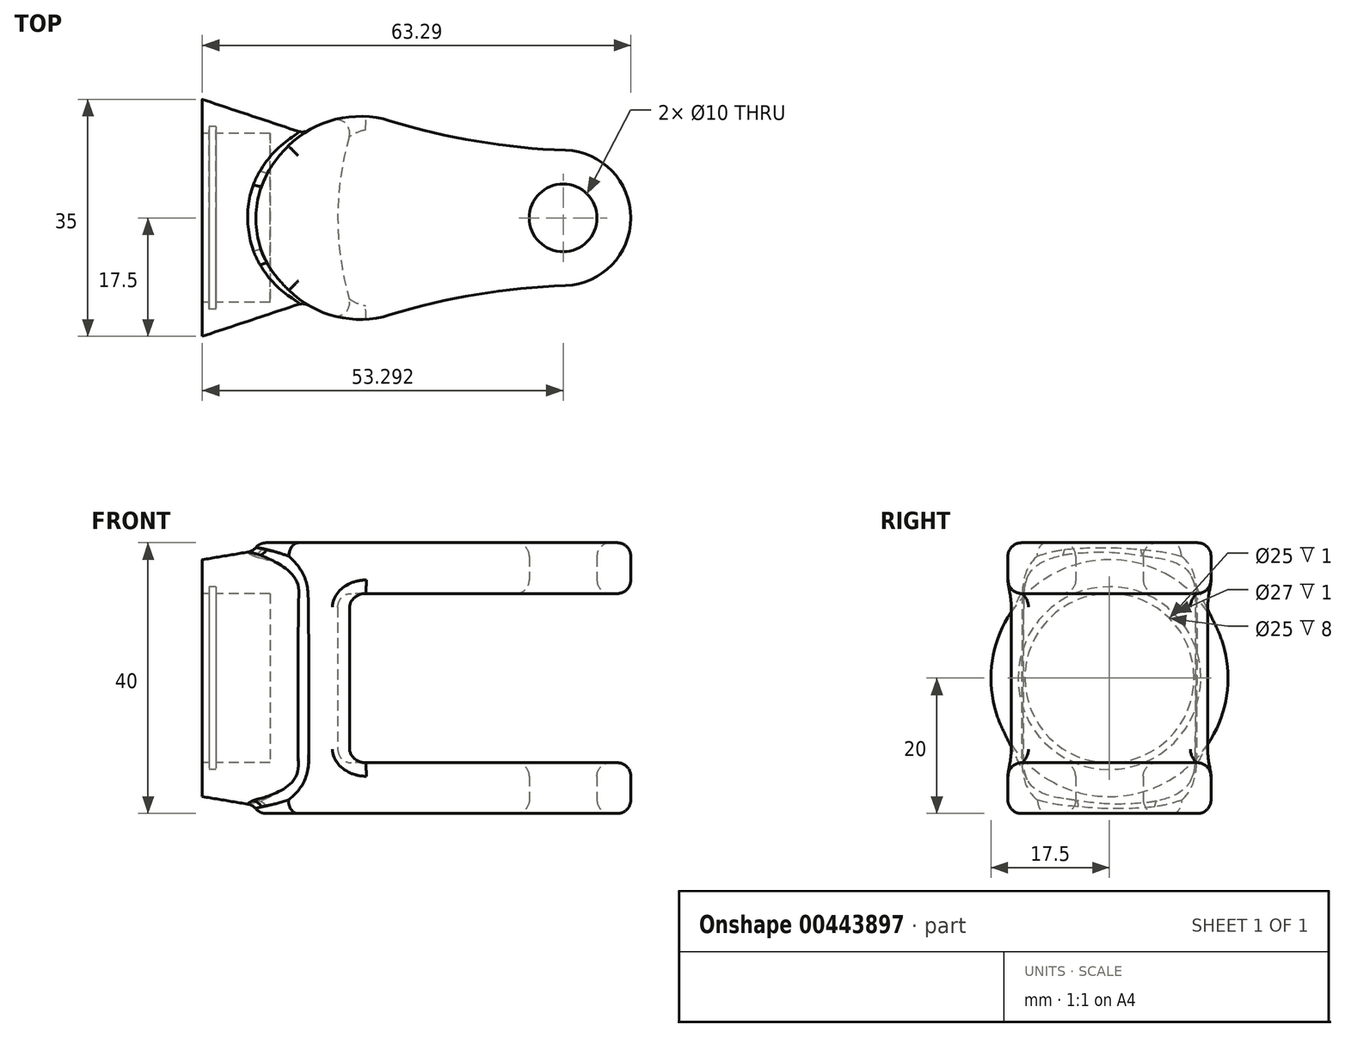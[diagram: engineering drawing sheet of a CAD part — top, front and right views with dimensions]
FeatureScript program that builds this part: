
annotation { "Feature Type Name" : "Feature", "Feature Type Description" : "" }
export const myFeature = defineFeature(function(context is Context, id is Id, definition is map)
    precondition{}
    {
        {
            var Q0;
            Q0=qCreatedBy(makeId("Right.planeOp"),FACE);
            var sketch = newSketch(context, id + "F0", { "sketchPlane" : qUnion([Q0])});
            skCircle(sketch, "E0", {"center": v(0, 0) * mm, "radius": 17.5 * mm});
            skSolve(sketch);
        }
        {
            var Q0;
            Q0=qCreatedBy(makeId("Right.planeOp"),FACE);
            cPlane(context, id + "F1", {"entities" : qUnion([Q0]), "cplaneType" : CPlaneType.OFFSET, "offset" : 15 * mm, "width" : 150 * mm, "height" : 150 * mm});
        }
        {
            var Q0;
            Q0=qCreatedBy(id+"F1.planeOp",FACE);
            var sketch = newSketch(context, id + "F2", { "sketchPlane" : qUnion([Q0])});
            skLineSegment(sketch, "E1.bottom", {"start": v(-5, 20) * mm, "end": v(5, 20) * mm});
            skLineSegment(sketch, "E1.top", {"start": v(-5, -20) * mm, "end": v(5, -20) * mm});
            skLineSegment(sketch, "E1.left", {"start": v(-12.5, 12.5) * mm, "end": v(-12.5, -12.5) * mm});
            skLineSegment(sketch, "E1.right", {"start": v(12.5, 12.5) * mm, "end": v(12.5, -12.5) * mm});
            skPoint(sketch, "E1.middle", {"position": v(0, 0) * mm});
            skPoint(sketch, "E2.visualSharp", {"position": v(-12.5, 20) * mm});
            skArc(sketch, "E2.filletArc", {"start": v(-5, 20) * mm, "mid": v(-10.3, 17.8) * mm, "end": v(-12.5, 12.5) * mm});
            skPoint(sketch, "E3.visualSharp", {"position": v(12.5, 20) * mm});
            skArc(sketch, "E3.filletArc", {"start": v(12.5, 12.5) * mm, "mid": v(10.3, 17.8) * mm, "end": v(5, 20) * mm});
            skPoint(sketch, "E4.visualSharp", {"position": v(12.5, -20) * mm});
            skArc(sketch, "E4.filletArc", {"start": v(5, -20) * mm, "mid": v(10.3, -17.8) * mm, "end": v(12.5, -12.5) * mm});
            skPoint(sketch, "E5.visualSharp", {"position": v(-12.5, -20) * mm});
            skArc(sketch, "E5.filletArc", {"start": v(-12.5, -12.5) * mm, "mid": v(-10.3, -17.8) * mm, "end": v(-5, -20) * mm});
            skSolve(sketch);
        }
        {
            var Q0;
            Q0=makeQuery(id+"F0.imprint","IMPRINT",FACE,{"disambiguationData":[TD([[makeQuery(id+"F0.imprint","IMPRINT",EDGE,{"derivedFrom":sQuery(id+"F0.wireOp",EDGE,"E0")}),1.0]])]});
            var Q1;
            Q1=makeQuery(id+"F2.imprint","IMPRINT",FACE,{"disambiguationData":[TD([[makeQuery(id+"F2.imprint","IMPRINT",EDGE,{"derivedFrom":sQuery(id+"F2.wireOp",EDGE,"E1.bottom")}),-1.0]])]});
            loft(context, id + "F3", {"sheetProfilesArray" : [{ "sheetProfileEntities" : qUnion([Q0]) }, { "sheetProfileEntities" : qUnion([Q1]) }]});
        }
        {
            var Q0;
            Q0=qCreatedBy(makeId("Top.planeOp"),FACE);
            var sketch = newSketch(context, id + "F4", { "sketchPlane" : qUnion([Q0])});
            skCircle(sketch, "E6", {"center": v(23.3, 0) * mm, "radius": 15 * mm});
            skCircle(sketch, "E7", {"center": v(53.3, 0) * mm, "radius": 10 * mm});
            skArc(sketch, "E8", {"start": v(27.7, -14.34) * mm, "mid": v(40.52, -11.31) * mm, "end": v(53.63, -10) * mm});
            skArc(sketch, "E9", {"start": v(27.7, 14.34) * mm, "mid": v(40.52, 11.31) * mm, "end": v(53.63, 10) * mm});
            skSolve(sketch);
        }
        {
            var Q0;
            Q0 = qSketchRegion(id + "F4", true);
            extrude(context, id + "F5", {"entities" : qUnion([Q0]), "operationType" : NewBodyOperationType.ADD, "endBound" : BoundingType.SYMMETRIC, "depth" : 40 * mm});
        }
        {
            var Q0;
            Q0=qCreatedBy(makeId("Front.planeOp"),FACE);
            var sketch = newSketch(context, id + "F6", { "sketchPlane" : qUnion([Q0])});
            skLineSegment(sketch, "E10.0.0", {"start": v(53.63, -20) * mm, "end": v(63.3, -20) * mm});
            skLineSegment(sketch, "E10.0.1", {"start": v(53.63, -20) * mm, "end": v(53.63, 20) * mm});
            skLineSegment(sketch, "E10.0.2", {"start": v(53.63, 20) * mm, "end": v(63.3, 20) * mm});
            skLineSegment(sketch, "E10.0.3", {"start": v(53.63, 20) * mm, "end": v(53.63, -20) * mm});
            skLineSegment(sketch, "E11.bottom", {"start": v(63.3, 12.5) * mm, "end": v(20, 12.5) * mm});
            skLineSegment(sketch, "E11.top", {"start": v(63.3, -12.5) * mm, "end": v(20, -12.5) * mm});
            skLineSegment(sketch, "E11.left", {"start": v(63.3, 12.5) * mm, "end": v(63.3, -12.5) * mm});
            skLineSegment(sketch, "E11.right", {"start": v(20, 12.5) * mm, "end": v(20, -12.5) * mm});
            skSolve(sketch);
        }
        {
            var Q0;
            Q0 = qSketchRegion(id + "F6", true);
            var Q1;
            Q1=sQuery(id+"F6.wireOp",EDGE,"E11.left");
            revolve(context, id + "F7", {"operationType" : NewBodyOperationType.REMOVE, "entities" : qUnion([Q0]), "axis" : qUnion([Q1]), "revolveType" : RevolveType.FULL, "oppositeDirection" : true});
        }
        {
            var Q0;
            Q0=makeQuery(id+"F3.opLoft","CAP_FACE",FACE,{"disambiguationData":[OSD([makeQuery(id+"F0.imprint","IMPRINT",FACE,{"disambiguationData":[TD([[makeQuery(id+"F0.imprint","IMPRINT",EDGE,{"derivedFrom":sQuery(id+"F0.wireOp",EDGE,"E0")}),1.0]])]})])],"isStart":true});
            var sketch = newSketch(context, id + "F8", { "sketchPlane" : qUnion([Q0])});
            skCircle(sketch, "E12", {"center": v(0, 0) * mm, "radius": 12.5 * mm});
            skSolve(sketch);
        }
        {
            var Q0;
            Q0 = qSketchRegion(id + "F8", true);
            extrude(context, id + "F9", {"entities" : qUnion([Q0]), "operationType" : NewBodyOperationType.REMOVE, "oppositeDirection" : true, "depth" : 10 * mm});
        }
        {
            var Q0;
            Q0=makeQuery(id+"F3.opLoft","CAP_FACE",FACE,{"disambiguationData":[OSD([makeQuery(id+"F0.imprint","IMPRINT",FACE,{"disambiguationData":[TD([[makeQuery(id+"F0.imprint","IMPRINT",EDGE,{"derivedFrom":sQuery(id+"F0.wireOp",EDGE,"E0")}),1.0]])]})])],"isStart":true});
            cPlane(context, id + "F10", {"entities" : qUnion([Q0]), "cplaneType" : CPlaneType.OFFSET, "offset" : 1 * mm, "oppositeDirection" : true, "width" : 150 * mm, "height" : 150 * mm});
        }
        {
            var Q0;
            Q0=qCreatedBy(id+"F10.planeOp",FACE);
            var sketch = newSketch(context, id + "F11", { "sketchPlane" : qUnion([Q0])});
            skCircle(sketch, "E13.0", {"center": v(0, 0) * mm, "radius": 13.5 * mm});
            skSolve(sketch);
        }
        {
            var Q0;
            Q0 = qSketchRegion(id + "F11", true);
            extrude(context, id + "F12", {"entities" : qUnion([Q0]), "operationType" : NewBodyOperationType.REMOVE, "oppositeDirection" : true, "depth" : 1 * mm});
        }
        {
            var Q0;
            Q0=makeQuery(id+"F5.opExtrude","CAP_FACE",FACE,{"disambiguationData":[OSD([sQuery(id+"F4.wireOp",EDGE,"E6"),sQuery(id+"F4.wireOp",EDGE,"E7"),sQuery(id+"F4.wireOp",EDGE,"E8"),sQuery(id+"F4.wireOp",EDGE,"E9")])],"isStart":true});
            var sketch = newSketch(context, id + "F13", { "sketchPlane" : qUnion([Q0])});
            skCircle(sketch, "E14", {"center": v(53.3, 0) * mm, "radius": 5 * mm});
            skSolve(sketch);
        }
        {
            var Q0;
            Q0=makeQuery(id+"F13.imprint","IMPRINT",FACE,{"disambiguationData":[TD([[makeQuery(id+"F13.imprint","IMPRINT",EDGE,{"derivedFrom":sQuery(id+"F13.wireOp",EDGE,"E14")}),1.0]])]});
            var Q1;
            Q1=sQuery(id+"F13.wireOp",EDGE,"E14");
            extrude(context, id + "F14", {"entities" : qUnion([Q0]), "operationType" : NewBodyOperationType.REMOVE, "surfaceEntities" : qUnion([Q1]), "endBound" : BoundingType.THROUGH_ALL, "oppositeDirection" : true, "depth" : 25 * mm});
        }
        {
            var Q0;
            Q0=makeQuery(id+"F7.boolean.opBoolean","COPY",EDGE,{"derivedFrom":makeQuery(id+"F7.opRevolve","SWEPT_EDGE",EDGE,{"disambiguationData":[OSD([sQuery(id+"F6.wireOp",EDGE,"E11.bottom"),sQuery(id+"F6.wireOp",EDGE,"E11.right")])]})});
            var Q1;
            Q1=makeQuery(id+"F7.boolean.opBoolean","COPY",EDGE,{"derivedFrom":makeQuery(id+"F7.opRevolve","SWEPT_EDGE",EDGE,{"disambiguationData":[OSD([sQuery(id+"F6.wireOp",EDGE,"E11.top"),sQuery(id+"F6.wireOp",EDGE,"E11.right")])]})});
            fillet(context, id + "F15", {"entities" : qUnion([Q0, Q1]), "radius" : 2 * mm, "tangentPropagation" : true, "allowEdgeOverflow" : false});
        }
        {
            var Q0;
            Q0=makeQuery(id+"F5.boolean.opBoolean","INTERSECT",EDGE,{"disambiguationData":[OD(1.0)],"derivedFrom":[makeQuery(id+"F3.opLoft","SWEPT_FACE",FACE,{"disambiguationData":[OSD([sQuery(id+"F0.wireOp",EDGE,"E0"),sQuery(id+"F2.wireOp",EDGE,"E1.bottom"),sQuery(id+"F2.wireOp",EDGE,"E1.left"),sQuery(id+"F2.wireOp",EDGE,"E2.filletArc")])]}),makeQuery(id+"F5.opExtrude","SWEPT_FACE",FACE,{"disambiguationData":[OSD([sQuery(id+"F4.wireOp",EDGE,"E6")])]})]});
            var Q1;
            Q1=makeQuery(id+"F5.boolean.opBoolean","INTERSECT",EDGE,{"disambiguationData":[OD(0.0)],"derivedFrom":[makeQuery(id+"F3.opLoft","SWEPT_FACE",FACE,{"disambiguationData":[OSD([sQuery(id+"F0.wireOp",EDGE,"E0"),sQuery(id+"F2.wireOp",EDGE,"E1.bottom"),sQuery(id+"F2.wireOp",EDGE,"E1.left"),sQuery(id+"F2.wireOp",EDGE,"E2.filletArc")])]}),makeQuery(id+"F5.opExtrude","SWEPT_FACE",FACE,{"disambiguationData":[OSD([sQuery(id+"F4.wireOp",EDGE,"E6")])]})]});
            fillet(context, id + "F16", {"entities" : qUnion([Q0, Q1]), "radius" : 2 * mm, "tangentPropagation" : true, "allowEdgeOverflow" : false});
        }
        {
            var Q0;
            Q0=makeQuery(id+"F5.opExtrude","CAP_FACE",FACE,{"disambiguationData":[OSD([sQuery(id+"F4.wireOp",EDGE,"E6"),sQuery(id+"F4.wireOp",EDGE,"E7"),sQuery(id+"F4.wireOp",EDGE,"E8"),sQuery(id+"F4.wireOp",EDGE,"E9")])],"isStart":true});
            var Q1;
            Q1=makeQuery(id+"F5.opExtrude","CAP_FACE",FACE,{"disambiguationData":[OSD([sQuery(id+"F4.wireOp",EDGE,"E6"),sQuery(id+"F4.wireOp",EDGE,"E7"),sQuery(id+"F4.wireOp",EDGE,"E8"),sQuery(id+"F4.wireOp",EDGE,"E9")])],"isStart":false});
            fillet(context, id + "F17", {"entities" : qUnion([Q0, Q1]), "radius" : 2 * mm, "tangentPropagation" : true, "allowEdgeOverflow" : false});
        }
        {
            var Q0;
            Q0=makeQuery(id+"F7.boolean.opBoolean","COPY",FACE,{"derivedFrom":makeQuery(id+"F7.opRevolve","SWEPT_FACE",FACE,{"disambiguationData":[OSD([sQuery(id+"F6.wireOp",EDGE,"E11.bottom")])]})});
            var Q1;
            Q1=makeQuery(id+"F7.boolean.opBoolean","COPY",FACE,{"derivedFrom":makeQuery(id+"F7.opRevolve","SWEPT_FACE",FACE,{"disambiguationData":[OSD([sQuery(id+"F6.wireOp",EDGE,"E11.top")])]})});
            fillet(context, id + "F18", {"entities" : qUnion([Q0, Q1]), "radius" : 2 * mm, "tangentPropagation" : true, "allowEdgeOverflow" : false});
        }
    });
